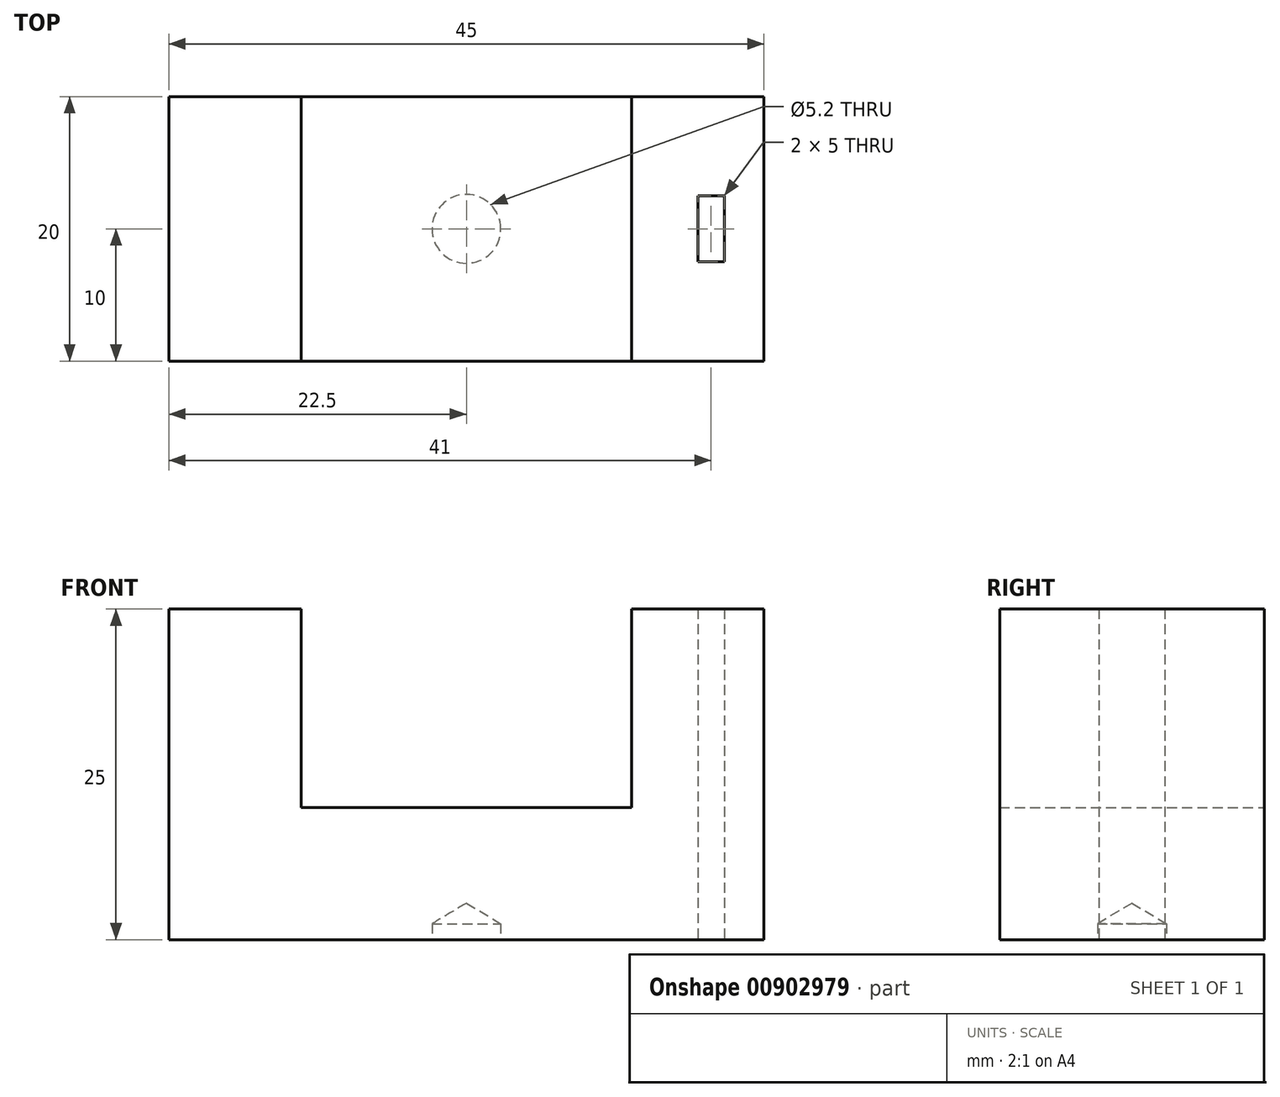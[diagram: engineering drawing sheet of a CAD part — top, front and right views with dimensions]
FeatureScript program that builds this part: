
annotation { "Feature Type Name" : "Feature", "Feature Type Description" : "" }
export const myFeature = defineFeature(function(context is Context, id is Id, definition is map)
    precondition{}
    {
        {
            var Q0;
            Q0=qCreatedBy(makeId("Top.planeOp"),FACE);
            var sketch = newSketch(context, id + "F0", { "sketchPlane" : qUnion([Q0])});
            skLineSegment(sketch, "E0.bottom", {"start": v(-12.5, 10) * mm, "end": v(12.5, 10) * mm});
            skLineSegment(sketch, "E0.top", {"start": v(-12.5, -10) * mm, "end": v(12.5, -10) * mm});
            skLineSegment(sketch, "E0.left", {"start": v(-12.5, 10) * mm, "end": v(-12.5, -10) * mm});
            skLineSegment(sketch, "E0.right", {"start": v(12.5, 10) * mm, "end": v(12.5, -10) * mm});
            skPoint(sketch, "E0.middle", {"position": v(0, 0) * mm});
            skLineSegment(sketch, "E1.bottom", {"start": v(-22.5, 10) * mm, "end": v(22.5, 10) * mm});
            skLineSegment(sketch, "E1.top", {"start": v(-22.5, -10) * mm, "end": v(22.5, -10) * mm});
            skLineSegment(sketch, "E1.left", {"start": v(-22.5, 10) * mm, "end": v(-22.5, -10) * mm});
            skLineSegment(sketch, "E1.right", {"start": v(22.5, 10) * mm, "end": v(22.5, -10) * mm});
            skSolve(sketch);
        }
        {
            var Q0;
            {var subQ0=sQuery(id+"F0.wireOp",EDGE,"E0.left");Q0=makeQuery(id+"F0.imprint","IMPRINT",FACE,{"disambiguationData":[TD([[makeQuery(id+"F0.imprint","IMPRINT",EDGE,{"derivedFrom":subQ0}),1.0]])]});}
            var Q1;
            {var subQ0=sQuery(id+"F0.wireOp",EDGE,"E0.left");Q1=makeQuery(id+"F0.imprint","IMPRINT",FACE,{"disambiguationData":[TD([[makeQuery(id+"F0.imprint","IMPRINT",EDGE,{"derivedFrom":subQ0}),-1.0]])]});}
            var Q2;
            {var subQ0=sQuery(id+"F0.wireOp",EDGE,"E0.right");Q2=makeQuery(id+"F0.imprint","IMPRINT",FACE,{"disambiguationData":[TD([[makeQuery(id+"F0.imprint","IMPRINT",EDGE,{"derivedFrom":subQ0}),1.0]])]});}
            extrude(context, id + "F1", {"entities" : qUnion([Q0, Q1, Q2]), "depth" : 10 * mm, "offsetDistance" : 25 * mm});
        }
        {
            var Q0;
            {var subQ0=sQuery(id+"F0.wireOp",EDGE,"E0.left");Q0=makeQuery(id+"F0.imprint","IMPRINT",FACE,{"disambiguationData":[TD([[makeQuery(id+"F0.imprint","IMPRINT",EDGE,{"derivedFrom":subQ0}),-1.0]])]});}
            var Q1;
            {var subQ0=sQuery(id+"F0.wireOp",EDGE,"E0.right");Q1=makeQuery(id+"F0.imprint","IMPRINT",FACE,{"disambiguationData":[TD([[makeQuery(id+"F0.imprint","IMPRINT",EDGE,{"derivedFrom":subQ0}),1.0]])]});}
            extrude(context, id + "F2", {"entities" : qUnion([Q0, Q1]), "operationType" : NewBodyOperationType.ADD, "depth" : 25 * mm, "offsetDistance" : 25 * mm});
        }
        {
            var Q0;
            Q0=makeQuery(id+"F1.opExtrude","CAP_FACE",FACE,{"disambiguationData":[OSD([sQuery(id+"F0.wireOp",EDGE,"E1.bottom"),sQuery(id+"F0.wireOp",EDGE,"E1.top"),sQuery(id+"F0.wireOp",EDGE,"E1.left"),sQuery(id+"F0.wireOp",EDGE,"E1.right")])],"isStart":true});
            var sketch = newSketch(context, id + "F3", { "sketchPlane" : qUnion([Q0])});
            skPoint(sketch, "E2", {"position": v(0, 0) * mm});
            skLineSegment(sketch, "E3.bottom", {"start": v(22.5, 10) * mm, "end": v(12.5, 10) * mm});
            skLineSegment(sketch, "E3.top", {"start": v(22.5, -10) * mm, "end": v(12.5, -10) * mm});
            skLineSegment(sketch, "E3.left", {"start": v(22.5, 10) * mm, "end": v(22.5, -10) * mm});
            skLineSegment(sketch, "E3.right", {"start": v(12.5, 10) * mm, "end": v(12.5, -10) * mm});
            skLineSegment(sketch, "E4", {"start": v(12.5, 0) * mm, "end": v(22.5, 0) * mm});
            skPoint(sketch, "E5", {"position": v(19.5, 0) * mm});
            skPoint(sketch, "E6", {"position": v(17.5, 0) * mm});
            skPoint(sketch, "E7", {"position": v(18.5, 0) * mm});
            skLineSegment(sketch, "E8.bottom", {"start": v(17.5, 2.5) * mm, "end": v(19.5, 2.5) * mm});
            skLineSegment(sketch, "E8.top", {"start": v(17.5, -2.5) * mm, "end": v(19.5, -2.5) * mm});
            skLineSegment(sketch, "E8.left", {"start": v(17.5, 2.5) * mm, "end": v(17.5, -2.5) * mm});
            skLineSegment(sketch, "E8.right", {"start": v(19.5, 2.5) * mm, "end": v(19.5, -2.5) * mm});
            skSolve(sketch);
        }
        {
            var Q0;
            Q0=sQuery(id+"F3.wireOp",VERTEX,"E2");
            var Q1;
            Q1=makeQuery(id+"F1.opExtrude","SWEPT_BODY",BODY,{"disambiguationData":[OSD([sQuery(id+"F0.wireOp",EDGE,"E1.bottom"),sQuery(id+"F0.wireOp",EDGE,"E1.top"),sQuery(id+"F0.wireOp",EDGE,"E1.left"),sQuery(id+"F0.wireOp",EDGE,"E1.right")])]});
            hole(context, id + "F4", {"style" : HoleStyle.SIMPLE, "endStyle" : HoleEndStyle.BLIND, "holeDiameter" : 5.2 * mm, "majorDiameter" : 5 * mm, "holeDepth" : 1.2 * mm, "isTappedThrough" : true, "tappedDepth" : 12 * mm, "tapClearance" : 3, "locations" : qUnion([Q0]), "scope" : qUnion([Q1])});
        }
        {
            var Q0;
            {var subQ5=sQuery(id+"F3.wireOp",EDGE,"E8.bottom");Q0=makeQuery(id+"F3.imprint","IMPRINT",FACE,{"disambiguationData":[TD([[makeQuery(id+"F3.imprint","IMPRINT",EDGE,{"derivedFrom":subQ5}),-1.0]])]});}
            var Q1;
            {var subQ5=sQuery(id+"F3.wireOp",EDGE,"E8.top");Q1=makeQuery(id+"F3.imprint","IMPRINT",FACE,{"disambiguationData":[TD([[makeQuery(id+"F3.imprint","IMPRINT",EDGE,{"derivedFrom":subQ5}),1.0]])]});}
            extrude(context, id + "F5", {"entities" : qUnion([Q0, Q1]), "operationType" : NewBodyOperationType.REMOVE, "oppositeDirection" : true, "depth" : 36.07 * mm, "offsetDistance" : 25 * mm});
        }
    });
